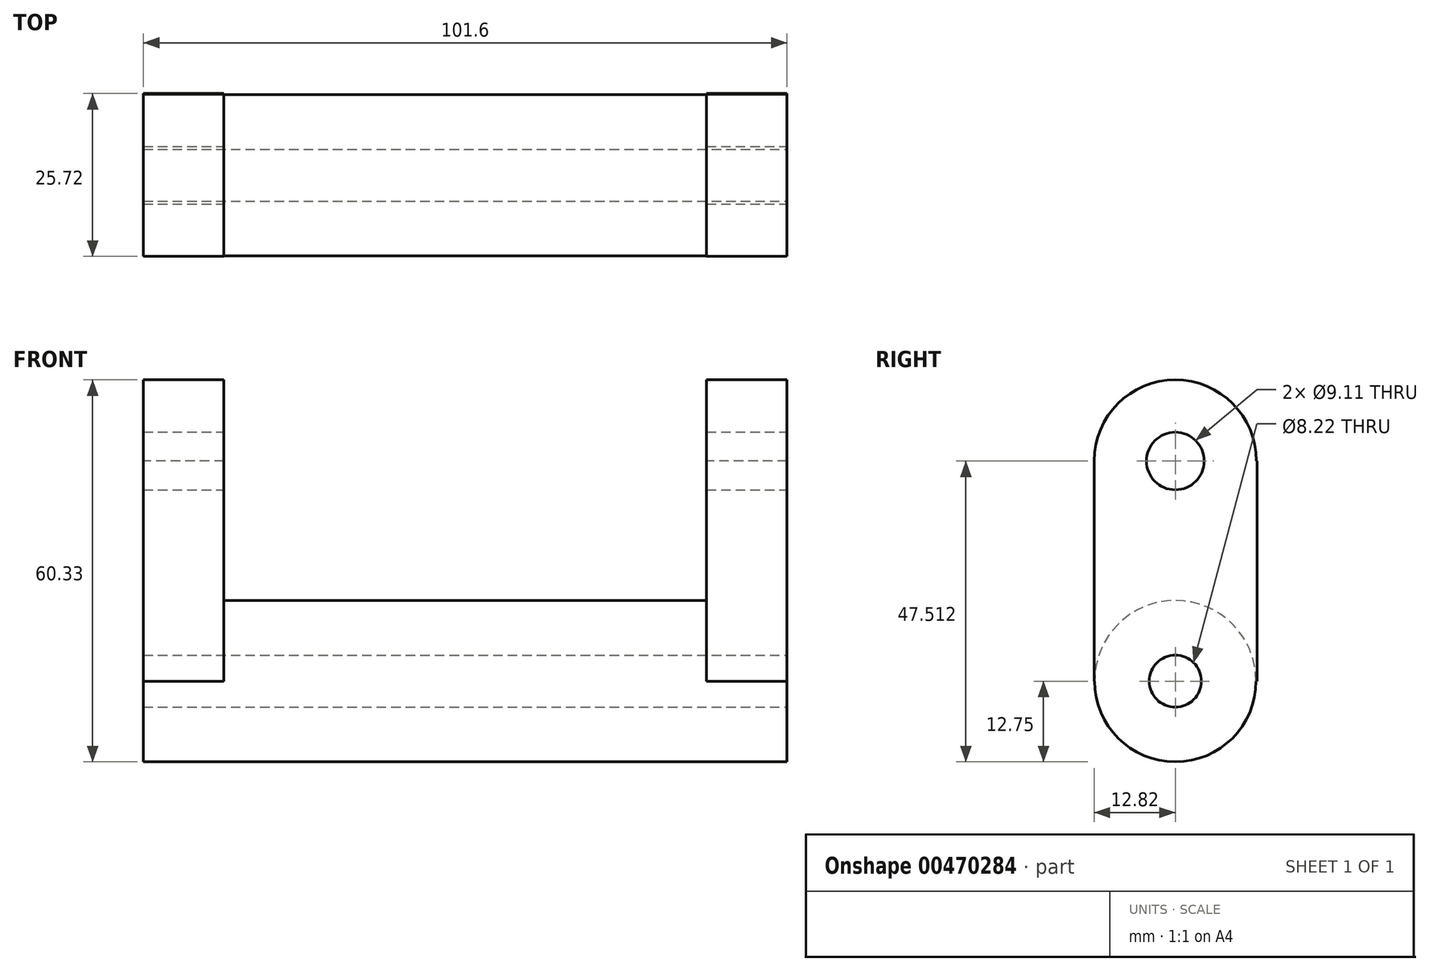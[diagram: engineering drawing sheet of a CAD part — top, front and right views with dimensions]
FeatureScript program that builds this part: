
annotation { "Feature Type Name" : "Feature", "Feature Type Description" : "" }
export const myFeature = defineFeature(function(context is Context, id is Id, definition is map)
    precondition{}
    {
        {
            var Q0;
            Q0=qCreatedBy(makeId("Right.planeOp"),FACE);
            var sketch = newSketch(context, id + "F0", { "sketchPlane" : qUnion([Q0])});
            skCircle(sketch, "E0", {"center": v(0, 0) * mm, "radius": 12.75 * mm});
            skSolve(sketch);
        }
        {
            var Q0;
            Q0=qCreatedBy(makeId("Right.planeOp"),FACE);
            var sketch = newSketch(context, id + "F1", { "sketchPlane" : qUnion([Q0])});
            skCircle(sketch, "E1", {"center": v(0, 34.76) * mm, "radius": 12.82 * mm});
            skLineSegment(sketch, "E2.bottom", {"start": v(-12.82, 34.76) * mm, "end": v(12.9, 34.76) * mm});
            skLineSegment(sketch, "E2.top", {"start": v(-12.82, 0) * mm, "end": v(12.9, 0) * mm});
            skLineSegment(sketch, "E2.left", {"start": v(-12.82, 34.76) * mm, "end": v(-12.82, 0) * mm});
            skLineSegment(sketch, "E2.right", {"start": v(12.9, 34.76) * mm, "end": v(12.9, 0) * mm});
            skSolve(sketch);
        }
        {
            var Q0;
            Q0 = qSketchRegion(id + "F0", true);
            extrude(context, id + "F2", {"entities" : qUnion([Q0]), "depth" : 50.8 * mm});
        }
        {
            var Q0;
            Q0=makeQuery(id+"F2.opExtrude","SWEPT_BODY",BODY,{"disambiguationData":[OSD([sQuery(id+"F0.wireOp",EDGE,"E0")])]});
            var Q1;
            Q1=qCreatedBy(makeId("Right.planeOp"),FACE);
            mirror(context, id + "F3", {"operationType" : NewBodyOperationType.ADD, "entities" : qUnion([Q0]), "mirrorPlane" : qUnion([Q1])});
        }
        {
            var Q0;
            Q0 = qSketchRegion(id + "F1", true);
            extrude(context, id + "F4", {"entities" : qUnion([Q0]), "operationType" : NewBodyOperationType.ADD, "depth" : 50.8 * mm});
        }
        {
            var Q0;
            Q0=makeQuery(id+"F2.opExtrude","SWEPT_BODY",BODY,{"disambiguationData":[OSD([sQuery(id+"F0.wireOp",EDGE,"E0")])]});
            var Q1;
            Q1=qCreatedBy(makeId("Right.planeOp"),FACE);
            mirror(context, id + "F5", {"operationType" : NewBodyOperationType.ADD, "entities" : qUnion([Q0]), "mirrorPlane" : qUnion([Q1])});
        }
        {
            var Q0;
            Q0 = qSketchRegion(id + "F1", true);
            extrude(context, id + "F6", {"entities" : qUnion([Q0]), "operationType" : NewBodyOperationType.REMOVE, "endBound" : BoundingType.SYMMETRIC, "oppositeDirection" : true, "depth" : 76.2 * mm});
        }
        {
            var Q0;
            Q0 = qSketchRegion(id + "F0", true);
            extrude(context, id + "F7", {"entities" : qUnion([Q0]), "operationType" : NewBodyOperationType.ADD, "endBound" : BoundingType.SYMMETRIC, "depth" : 101.6 * mm});
        }
        {
            var Q0;
            Q0=makeQuery(id+"F4.boolean.opBoolean","MERGE",FACE,{"derivedFrom":[makeQuery(id+"F2.opExtrude","CAP_FACE",FACE,{"disambiguationData":[OSD([sQuery(id+"F0.wireOp",EDGE,"E0")])],"isStart":false}),makeQuery(id+"F4.opExtrude","CAP_FACE",FACE,{"disambiguationData":[OSD([sQuery(id+"F1.wireOp",EDGE,"E1"),sQuery(id+"F1.wireOp",EDGE,"E2.bottom"),sQuery(id+"F1.wireOp",EDGE,"E2.top"),sQuery(id+"F1.wireOp",EDGE,"E2.left"),sQuery(id+"F1.wireOp",EDGE,"E2.right")])],"isStart":false})]});
            var sketch = newSketch(context, id + "F8", { "sketchPlane" : qUnion([Q0])});
            skCircle(sketch, "E3", {"center": v(0, 34.76) * mm, "radius": 4.55 * mm});
            skCircle(sketch, "E4", {"center": v(0, 0) * mm, "radius": 4.11 * mm});
            skSolve(sketch);
        }
        {
            var Q0;
            Q0=makeQuery(id+"F8.imprint","IMPRINT",FACE,{"disambiguationData":[TD([[makeQuery(id+"F8.imprint","IMPRINT",EDGE,{"derivedFrom":sQuery(id+"F8.wireOp",EDGE,"E3")}),1.0]])]});
            var Q1;
            Q1=makeQuery(id+"F8.imprint","IMPRINT",FACE,{"disambiguationData":[TD([[makeQuery(id+"F8.imprint","IMPRINT",EDGE,{"derivedFrom":sQuery(id+"F8.wireOp",EDGE,"E4")}),1.0]])]});
            extrude(context, id + "F9", {"entities" : qUnion([Q0, Q1]), "operationType" : NewBodyOperationType.REMOVE, "endBound" : BoundingType.THROUGH_ALL, "oppositeDirection" : true, "depth" : 25.4 * mm});
        }
    });
